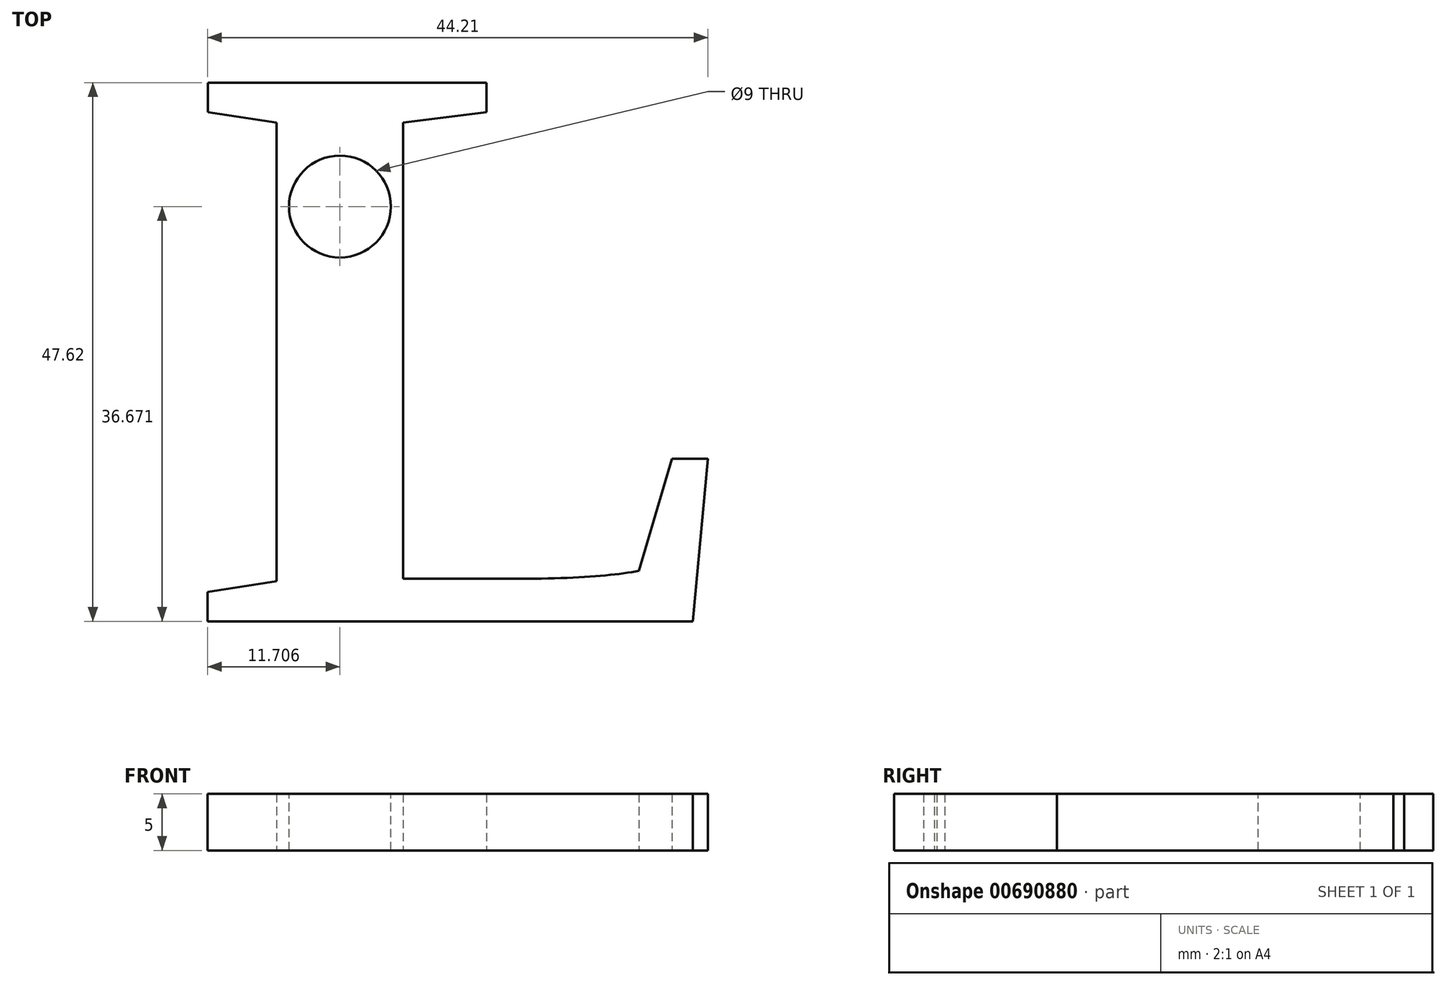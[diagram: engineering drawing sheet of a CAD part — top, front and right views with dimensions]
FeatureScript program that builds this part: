
annotation { "Feature Type Name" : "Feature", "Feature Type Description" : "" }
export const myFeature = defineFeature(function(context is Context, id is Id, definition is map)
    precondition{}
    {
        {
            var Q0;
            Q0=qCreatedBy(makeId("Top.planeOp"),FACE);
            var sketch = newSketch(context, id + "F0", { "sketchPlane" : qUnion([Q0])});
            skText(sketch, "E0", { "text": "L", "fontName": "Tinos-Bold.ttf"});
            const initialGuessF0  = {"E0": [-0.04166, -0.02258, 1, 0, 0.05236]};
            skSetInitialGuess(sketch, initialGuessF0);
            skSolve(sketch);
        }
        {
            var Q0;
            Q0 = qSketchRegion(id + "F0", true);
            extrude(context, id + "F1", {"entities" : qUnion([Q0]), "depth" : 5 * mm, "offsetDistance" : 25 * mm});
        }
        {
            var Q0;
            Q0=makeQuery(id+"F1.opExtrude","CAP_FACE",FACE,{"disambiguationData":[OSD([sQuery(id+"F0.wireOp",EDGE,"E0.sketch_text.stroke-0"),sQuery(id+"F0.wireOp",EDGE,"E0.sketch_text.stroke-1"),sQuery(id+"F0.wireOp",EDGE,"E0.sketch_text.stroke-2"),sQuery(id+"F0.wireOp",EDGE,"E0.sketch_text.stroke-3"),sQuery(id+"F0.wireOp",EDGE,"E0.sketch_text.stroke-4"),sQuery(id+"F0.wireOp",EDGE,"E0.sketch_text.stroke-5"),sQuery(id+"F0.wireOp",EDGE,"E0.sketch_text.stroke-6"),sQuery(id+"F0.wireOp",EDGE,"E0.sketch_text.stroke-7"),sQuery(id+"F0.wireOp",EDGE,"E0.sketch_text.stroke-8"),sQuery(id+"F0.wireOp",EDGE,"E0.sketch_text.stroke-9"),sQuery(id+"F0.wireOp",EDGE,"E0.sketch_text.stroke-10"),sQuery(id+"F0.wireOp",EDGE,"E0.sketch_text.stroke-11"),sQuery(id+"F0.wireOp",EDGE,"E0.sketch_text.stroke-12"),sQuery(id+"F0.wireOp",EDGE,"E0.sketch_text.stroke-13"),sQuery(id+"F0.wireOp",EDGE,"E0.sketch_text.stroke-14")])],"isStart":false});
            var sketch = newSketch(context, id + "F2", { "sketchPlane" : qUnion([Q0])});
            skLineSegment(sketch, "E1", {"start": v(-34.3, 21.52) * mm, "end": v(-23.12, 21.52) * mm, "construction": true});
            skLineSegment(sketch, "E2", {"start": v(-23.12, 21.52) * mm, "end": v(-23.12, -18.82) * mm, "construction": true});
            skLineSegment(sketch, "E3", {"start": v(-23.12, -18.82) * mm, "end": v(-34.3, -19.02) * mm, "construction": true});
            skLineSegment(sketch, "E4", {"start": v(-34.3, -19.02) * mm, "end": v(-34.3, 21.52) * mm, "construction": true});
            skLineSegment(sketch, "E5", {"start": v(-23.12, 0) * mm, "end": v(-34.3, 1.35) * mm, "construction": true});
            skPoint(sketch, "E5.startSnap0", {"position": v(-23.12, 1.35) * mm});
            skPoint(sketch, "E5.endSnap0", {"position": v(-23.12, 1.35) * mm});
            skLineSegment(sketch, "E6", {"start": v(-34.3, 1.35) * mm, "end": v(-23.12, 1.35) * mm, "construction": true});
            skLineSegment(sketch, "E7", {"start": v(-23.12, 0) * mm, "end": v(-34.3, 0) * mm, "construction": true});
            skLineSegment(sketch, "E8", {"start": v(-34.3, 0) * mm, "end": v(-23.12, 1.35) * mm, "construction": true});
            skLineSegment(sketch, "E9", {"start": v(-28.71, 14.1) * mm, "end": v(-28.71, 0.68) * mm, "construction": true});
            skPoint(sketch, "E9.startSnap0", {"position": v(-28.71, 1.35) * mm});
            skLineSegment(sketch, "E10", {"start": v(-28.71, 0.68) * mm, "end": v(-34.3, 21.52) * mm, "construction": true});
            skLineSegment(sketch, "E11", {"start": v(-23.12, 21.52) * mm, "end": v(-28.71, 1.35) * mm, "construction": true});
            skSolve(sketch);
        }
        {
            var Q0;
            Q0=sQuery(id+"F2.wireOp",VERTEX,"E9.start");
            var Q1;
            Q1=makeQuery(id+"F1.opExtrude","SWEPT_BODY",BODY,{"disambiguationData":[OSD([sQuery(id+"F0.wireOp",EDGE,"E0.sketch_text.stroke-0"),sQuery(id+"F0.wireOp",EDGE,"E0.sketch_text.stroke-1"),sQuery(id+"F0.wireOp",EDGE,"E0.sketch_text.stroke-2"),sQuery(id+"F0.wireOp",EDGE,"E0.sketch_text.stroke-3"),sQuery(id+"F0.wireOp",EDGE,"E0.sketch_text.stroke-4"),sQuery(id+"F0.wireOp",EDGE,"E0.sketch_text.stroke-5"),sQuery(id+"F0.wireOp",EDGE,"E0.sketch_text.stroke-6"),sQuery(id+"F0.wireOp",EDGE,"E0.sketch_text.stroke-7"),sQuery(id+"F0.wireOp",EDGE,"E0.sketch_text.stroke-8"),sQuery(id+"F0.wireOp",EDGE,"E0.sketch_text.stroke-9"),sQuery(id+"F0.wireOp",EDGE,"E0.sketch_text.stroke-10"),sQuery(id+"F0.wireOp",EDGE,"E0.sketch_text.stroke-11"),sQuery(id+"F0.wireOp",EDGE,"E0.sketch_text.stroke-12"),sQuery(id+"F0.wireOp",EDGE,"E0.sketch_text.stroke-13"),sQuery(id+"F0.wireOp",EDGE,"E0.sketch_text.stroke-14")])]});
            hole(context, id + "F3", {"style" : HoleStyle.SIMPLE, "endStyle" : HoleEndStyle.THROUGH, "holeDiameter" : 9 * mm, "majorDiameter" : 5 * mm, "isTappedThrough" : true, "tappedDepth" : 12 * mm, "tapClearance" : 3, "locations" : qUnion([Q0]), "scope" : qUnion([Q1])});
        }
    });
